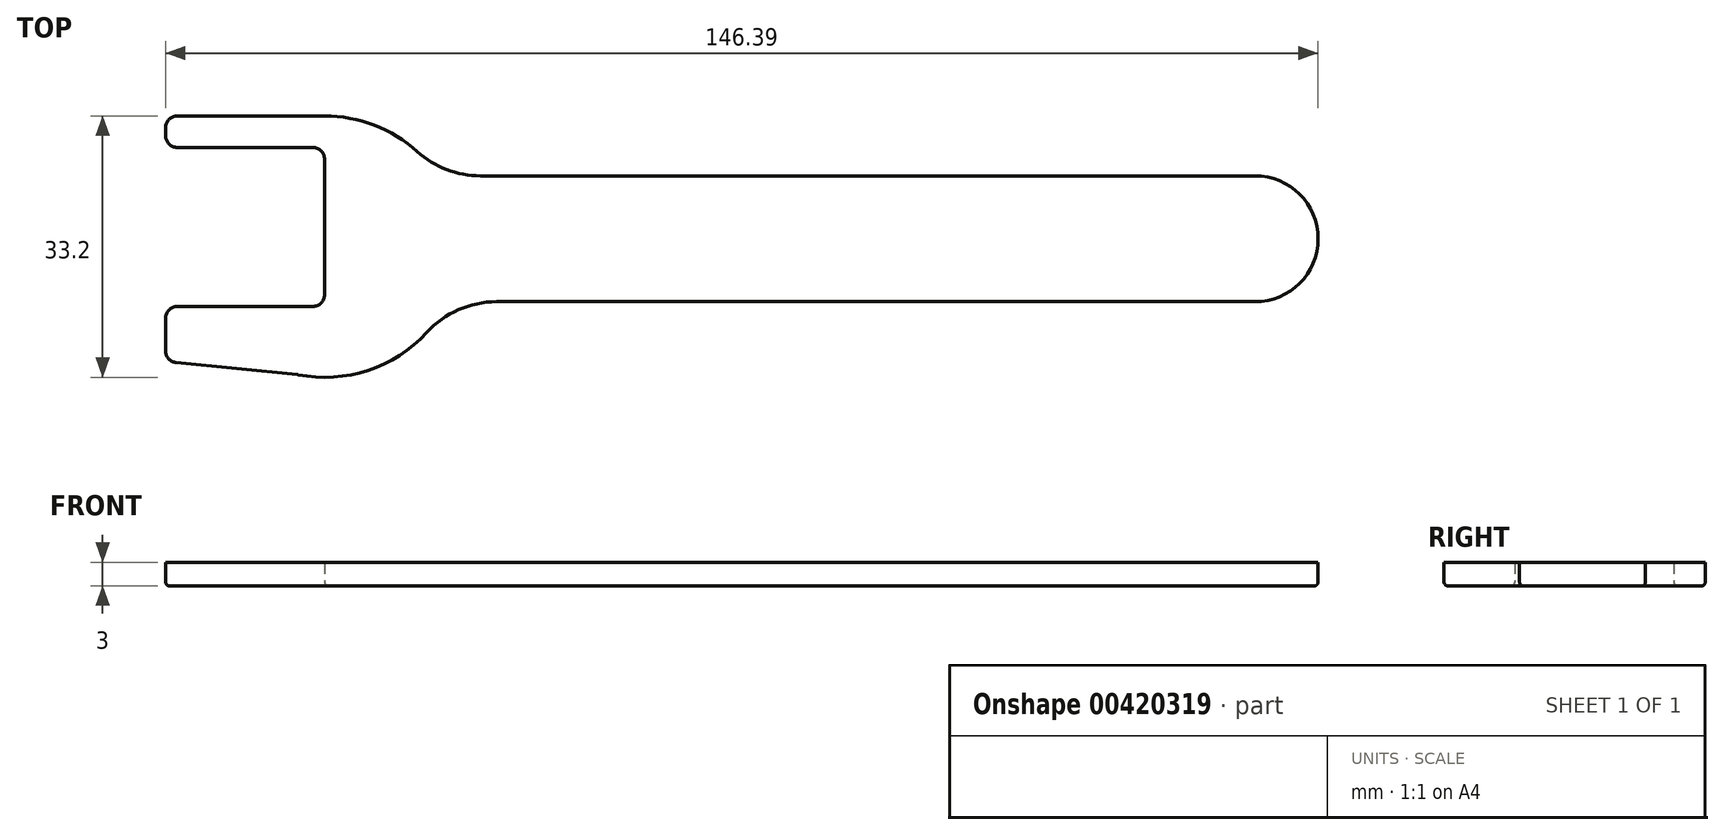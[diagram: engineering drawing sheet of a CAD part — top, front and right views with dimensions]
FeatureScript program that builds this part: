
annotation { "Feature Type Name" : "Feature", "Feature Type Description" : "" }
export const myFeature = defineFeature(function(context is Context, id is Id, definition is map)
    precondition{}
    {
        {
            var Q0;
            Q0=qCreatedBy(makeId("Top.planeOp"),FACE);
            var sketch = newSketch(context, id + "F0", { "sketchPlane" : qUnion([Q0])});
            skArc(sketch, "E0", {"start": v(-73.97, -17.26) * mm, "mid": v(-62.86, -15.84) * mm, "end": v(-54.85, -8) * mm});
            skLineSegment(sketch, "E1", {"start": v(59.4, -20.35) * mm, "end": v(59.4, 16.2) * mm, "construction": true});
            skLineSegment(sketch, "E2", {"start": v(-88.12, 35.8) * mm, "end": v(-88.12, -38.11) * mm, "construction": true});
            skLineSegment(sketch, "E3.top", {"start": v(-70.52, -17.6) * mm, "end": v(-50.32, -17.6) * mm, "construction": true});
            skLineSegment(sketch, "E3.left", {"start": v(-90.72, 15.6) * mm, "end": v(-90.72, 11.6) * mm});
            skLineSegment(sketch, "E3.right", {"start": v(-50.32, 17.6) * mm, "end": v(-50.32, -17.6) * mm, "construction": true});
            skLineSegment(sketch, "E4.top", {"start": v(-70.52, 11.6) * mm, "end": v(-90.72, 11.6) * mm});
            skLineSegment(sketch, "E5.top", {"start": v(-70.52, -8.6) * mm, "end": v(-90.72, -8.6) * mm});
            skLineSegment(sketch, "E5.right", {"start": v(-90.72, -15.6) * mm, "end": v(-90.72, -8.6) * mm});
            skLineSegment(sketch, "E6", {"start": v(-63.17, 15.6) * mm, "end": v(-90.72, 15.6) * mm});
            skLineSegment(sketch, "E7.trimOffspring", {"start": v(-90.72, -8.6) * mm, "end": v(-90.72, -15.6) * mm});
            skPoint(sketch, "E3.bottom.start.orphan", {"position": v(-90.72, 17.6) * mm});
            skLineSegment(sketch, "E8", {"start": v(-70.52, -17.6) * mm, "end": v(-90.72, -15.6) * mm});
            skPoint(sketch, "E9.orphan", {"position": v(-90.72, -17.6) * mm});
            skLineSegment(sketch, "E10", {"start": v(-70.52, -8.6) * mm, "end": v(-70.52, 11.6) * mm});
            skLineSegment(sketch, "E11", {"start": v(-98.89, 0) * mm, "end": v(66.7, 0) * mm, "construction": true});
            skArc(sketch, "E12", {"start": v(47.67, -8) * mm, "mid": v(55.67, 0) * mm, "end": v(47.67, 8) * mm});
            skLineSegment(sketch, "E13", {"start": v(47.67, 8) * mm, "end": v(-50.32, 8) * mm});
            skLineSegment(sketch, "E14", {"start": v(47.67, -8) * mm, "end": v(-54.85, -8) * mm});
            skPoint(sketch, "E15.end.orphan", {"position": v(-61.1, 8) * mm});
            skPoint(sketch, "E16.orphan", {"position": v(-62.74, 8) * mm});
            skArc(sketch, "E17.trimOffspring", {"start": v(-56.04, 8) * mm, "mid": v(-62.35, 13.58) * mm, "end": v(-70.52, 15.6) * mm});
            skLineSegment(sketch, "E18", {"start": v(-97.29, 15.6) * mm, "end": v(-46.92, 15.6) * mm, "construction": true});
            skLineSegment(sketch, "E19", {"start": v(-50.32, 8) * mm, "end": v(-56.04, 8) * mm});
            skSolve(sketch);
        }
        {
            var Q0;
            Q0=qSketchRegion(id+"F0",true);
            extrude(context, id + "F1", {"entities" : qUnion([Q0]), "depth" : 3 * mm});
        }
        {
            var Q0;
            Q0=makeQuery(id+"F1.opExtrude","SWEPT_EDGE",EDGE,{"disambiguationData":[OSD([sQuery(id+"F0.wireOp",EDGE,"E6"),sQuery(id+"F0.wireOp",EDGE,"E3.left")])]});
            var Q1;
            Q1=makeQuery(id+"F1.opExtrude","SWEPT_EDGE",EDGE,{"disambiguationData":[OSD([sQuery(id+"F0.wireOp",EDGE,"E4.top"),sQuery(id+"F0.wireOp",EDGE,"E3.left")])]});
            var Q2;
            Q2=makeQuery(id+"F1.opExtrude","SWEPT_EDGE",EDGE,{"disambiguationData":[OSD([sQuery(id+"F0.wireOp",EDGE,"E5.top"),sQuery(id+"F0.wireOp",EDGE,"E7.trimOffspring")])]});
            var Q3;
            Q3=makeQuery(id+"F1.opExtrude","SWEPT_EDGE",EDGE,{"disambiguationData":[OSD([sQuery(id+"F0.wireOp",EDGE,"E7.trimOffspring"),sQuery(id+"F0.wireOp",EDGE,"E8")])]});
            var Q4;
            Q4=makeQuery(id+"F1.opExtrude","SWEPT_EDGE",EDGE,{"disambiguationData":[OSD([sQuery(id+"F0.wireOp",EDGE,"E4.top"),sQuery(id+"F0.wireOp",EDGE,"E10")])]});
            var Q5;
            Q5=makeQuery(id+"F1.opExtrude","SWEPT_EDGE",EDGE,{"disambiguationData":[OSD([sQuery(id+"F0.wireOp",EDGE,"E5.top"),sQuery(id+"F0.wireOp",EDGE,"E10")])]});
            fillet(context, id + "F2", {"entities" : qUnion([Q0, Q1, Q2, Q3, Q4, Q5]), "radius" : 1.5 * mm, "tangentPropagation" : true, "allowEdgeOverflow" : false});
        }
        {
            var Q0;
            Q0=makeQuery(id+"F1.opExtrude","SWEPT_EDGE",EDGE,{"disambiguationData":[OSD([sQuery(id+"F0.wireOp",EDGE,"E13"),sQuery(id+"F0.wireOp",EDGE,"E17.trimOffspring")])]});
            var Q1;
            Q1=makeQuery(id+"F1.opExtrude","SWEPT_EDGE",EDGE,{"disambiguationData":[OSD([sQuery(id+"F0.wireOp",EDGE,"E0"),sQuery(id+"F0.wireOp",EDGE,"E14")])]});
            fillet(context, id + "F3", {"entities" : qUnion([Q0, Q1]), "radius" : 12 * mm, "tangentPropagation" : true, "allowEdgeOverflow" : false});
        }
        {
            var Q0;
            Q0=makeQuery(id+"F1.opExtrude","CAP_FACE",FACE,{"disambiguationData":[OSD([sQuery(id+"F0.wireOp",EDGE,"E0"),sQuery(id+"F0.wireOp",EDGE,"E4.top"),sQuery(id+"F0.wireOp",EDGE,"E5.top"),sQuery(id+"F0.wireOp",EDGE,"E6"),sQuery(id+"F0.wireOp",EDGE,"E3.left"),sQuery(id+"F0.wireOp",EDGE,"E7.trimOffspring"),sQuery(id+"F0.wireOp",EDGE,"E8"),sQuery(id+"F0.wireOp",EDGE,"E10"),sQuery(id+"F0.wireOp",EDGE,"E12"),sQuery(id+"F0.wireOp",EDGE,"E13"),sQuery(id+"F0.wireOp",EDGE,"E14"),sQuery(id+"F0.wireOp",EDGE,"E17.trimOffspring"),sQuery(id+"F0.wireOp",EDGE,"E19")])],"isStart":true});
            fillet(context, id + "F4", {"entities" : qUnion([Q0]), "radius" : .5 * mm, "tangentPropagation" : true, "allowEdgeOverflow" : false});
        }
    });
